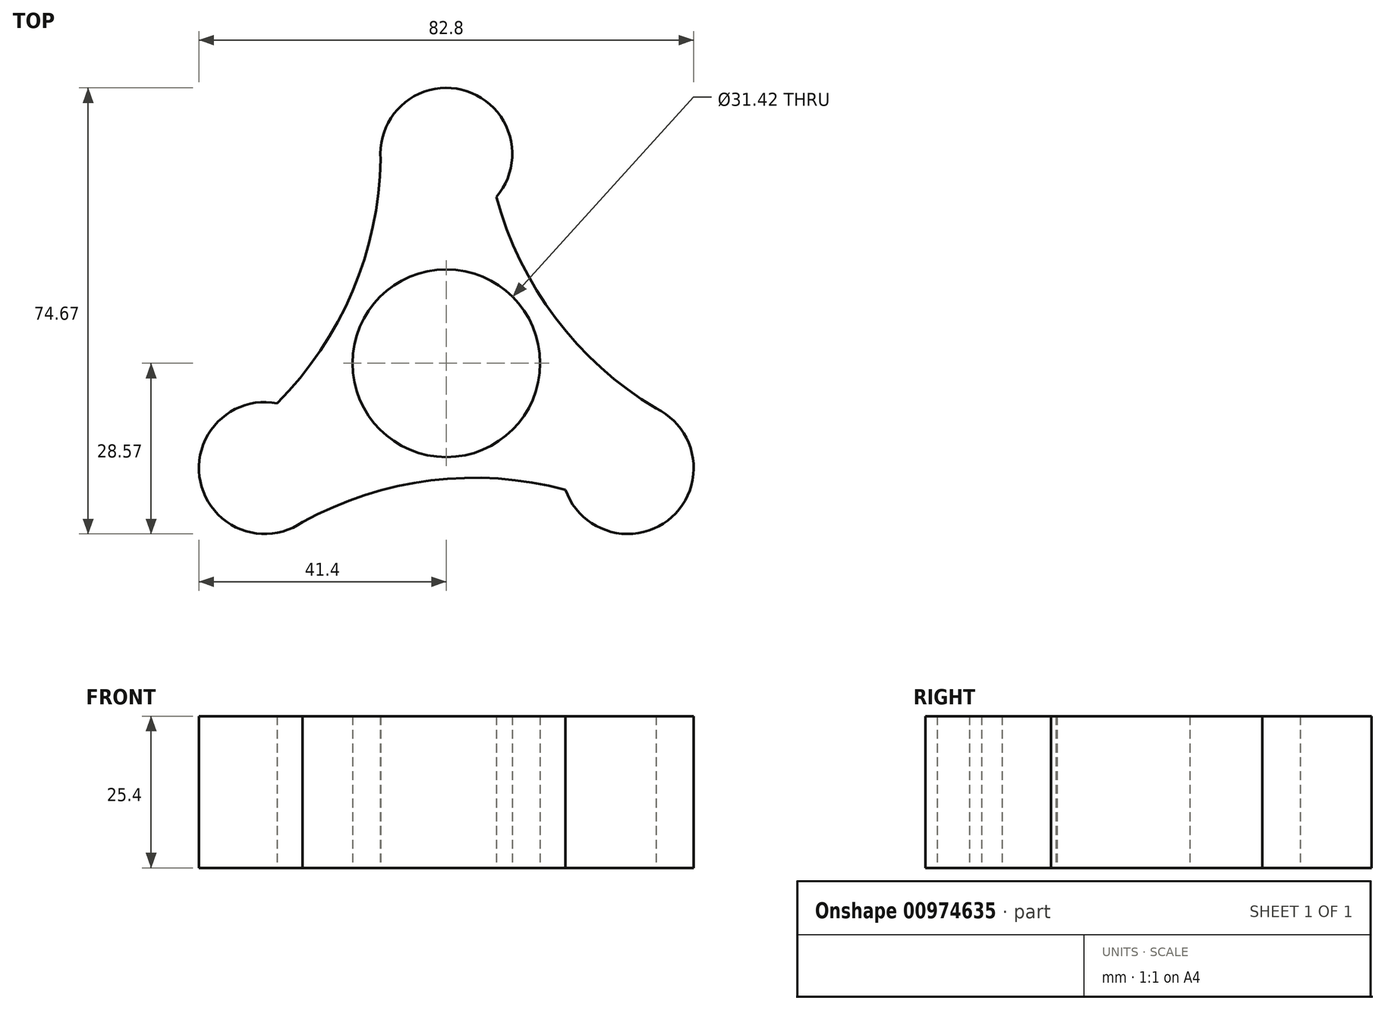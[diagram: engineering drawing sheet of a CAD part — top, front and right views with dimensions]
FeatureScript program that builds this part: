
annotation { "Feature Type Name" : "Feature", "Feature Type Description" : "" }
export const myFeature = defineFeature(function(context is Context, id is Id, definition is map)
    precondition{}
    {
        {
            var Q0;
            Q0=qCreatedBy(makeId("Top.planeOp"),FACE);
            var sketch = newSketch(context, id + "F0", { "sketchPlane" : qUnion([Q0])});
            skCircle(sketch, "E0", {"center": v(0, 0) * mm, "radius": 11.6 * mm});
            skCircle(sketch, "E1", {"center": v(0, 0) * mm, "radius": 15.7 * mm});
            skCircle(sketch, "E2", {"center": v(0, 35.06) * mm, "radius": 11.04 * mm});
            skCircle(sketch, "E3.1.0", {"center": v(-30.37, -17.53) * mm, "radius": 11.04 * mm});
            skCircle(sketch, "E3.2.0", {"center": v(30.37, -17.53) * mm, "radius": 11.04 * mm});
            skArc(sketch, "E4", {"start": v(-28.3, -6.7) * mm, "mid": v(-15.7, 12.06) * mm, "end": v(-11, 34.16) * mm});
            skArc(sketch, "E5.1.0", {"start": v(19.95, -21.17) * mm, "mid": v(-2.6, -19.62) * mm, "end": v(-24.08, -26.6) * mm});
            skArc(sketch, "E5.2.0", {"start": v(8.36, 27.86) * mm, "mid": v(18.3, 7.56) * mm, "end": v(35.08, -7.55) * mm});
            skSolve(sketch);
        }
        {
            var Q0;
            Q0 = qSketchRegion(id + "F0", true);
            extrude(context, id + "F1", {"entities" : qUnion([Q0]), "depth" : 25.4 * mm, "offsetDistance" : 25.4 * mm});
        }
    });
